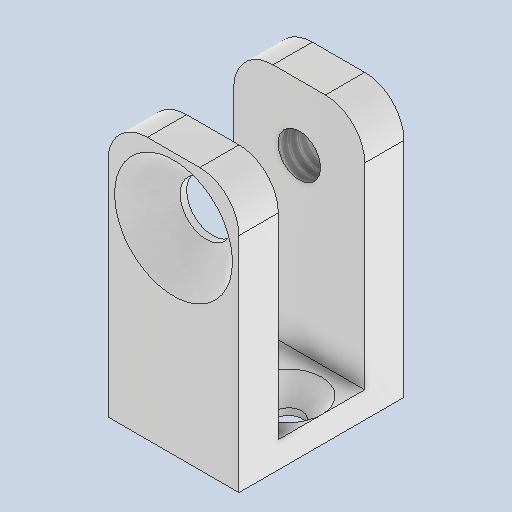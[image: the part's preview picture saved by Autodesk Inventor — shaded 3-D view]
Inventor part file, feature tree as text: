
AUTODESK INVENTOR PART (.ipt)
format: ipt  version: 2025 (Build 290162010, 162A)  size: 208,896 bytes
history: native  units: mm
features: sketch x5, hole x3, extrude x2, fillet x1
ambient origin geometry x8: Origin, YZ Plane, XZ Plane, XY Plane, X Axis, Y Axis, Z Axis, Center Point
bodies: Volumenkörper1 (feature_tree)
feature tree (11):
  extrude  "Extrusion1"  Depth=3.0mm
  fillet  "Rundung1"  Radius=3.0mm
  hole  "Bohrung1"  [1 undecoded]
  extrude  "Extrusion2"  Depth=2.0mm
  hole  "Bohrung2"  [1 undecoded]
  hole  "Bohrung3"  [1 undecoded]
  sketch  "Skizze1"  dims[d0=10.0mm d1=3.0mm d2=3.0mm]
  sketch  "Skizze2"  dims[d3=6.6mm d5=20.0mm d6=0.0mm]
  sketch  "Skizze3"  dims[d7=3.0mm]
  sketch  "Skizze4"  dims[d8=3.242mm d9=8.0mm d10=9.0mm d11=14.0mm d12=90.0deg d13=11.8mm d14=20.594885mm d15=2.0mm]
  sketch  "Skizze5"  dims[d16=20.0mm d17=0.0mm d19=2.0mm d20=8.0mm d21=5.0mm d22=2.0mm d23=90.0deg d24=8.0mm d25=20.594885mm d26=4.0mm d27=8.0mm d28=4.0mm d29=2.0mm d30=90.0deg d31=5.0mm d32=20.594885mm d34=5.0mm d35=9.0mm d36=6.3mm d37=5.0mm d38=9.0mm d40=9.0mm d41=0.0mm]
note: 3 required parameter values undecoded (feature->parameter linkage not recoverable at this tier; creation-order binding heuristic only, values carry confidence <= 0.55)
